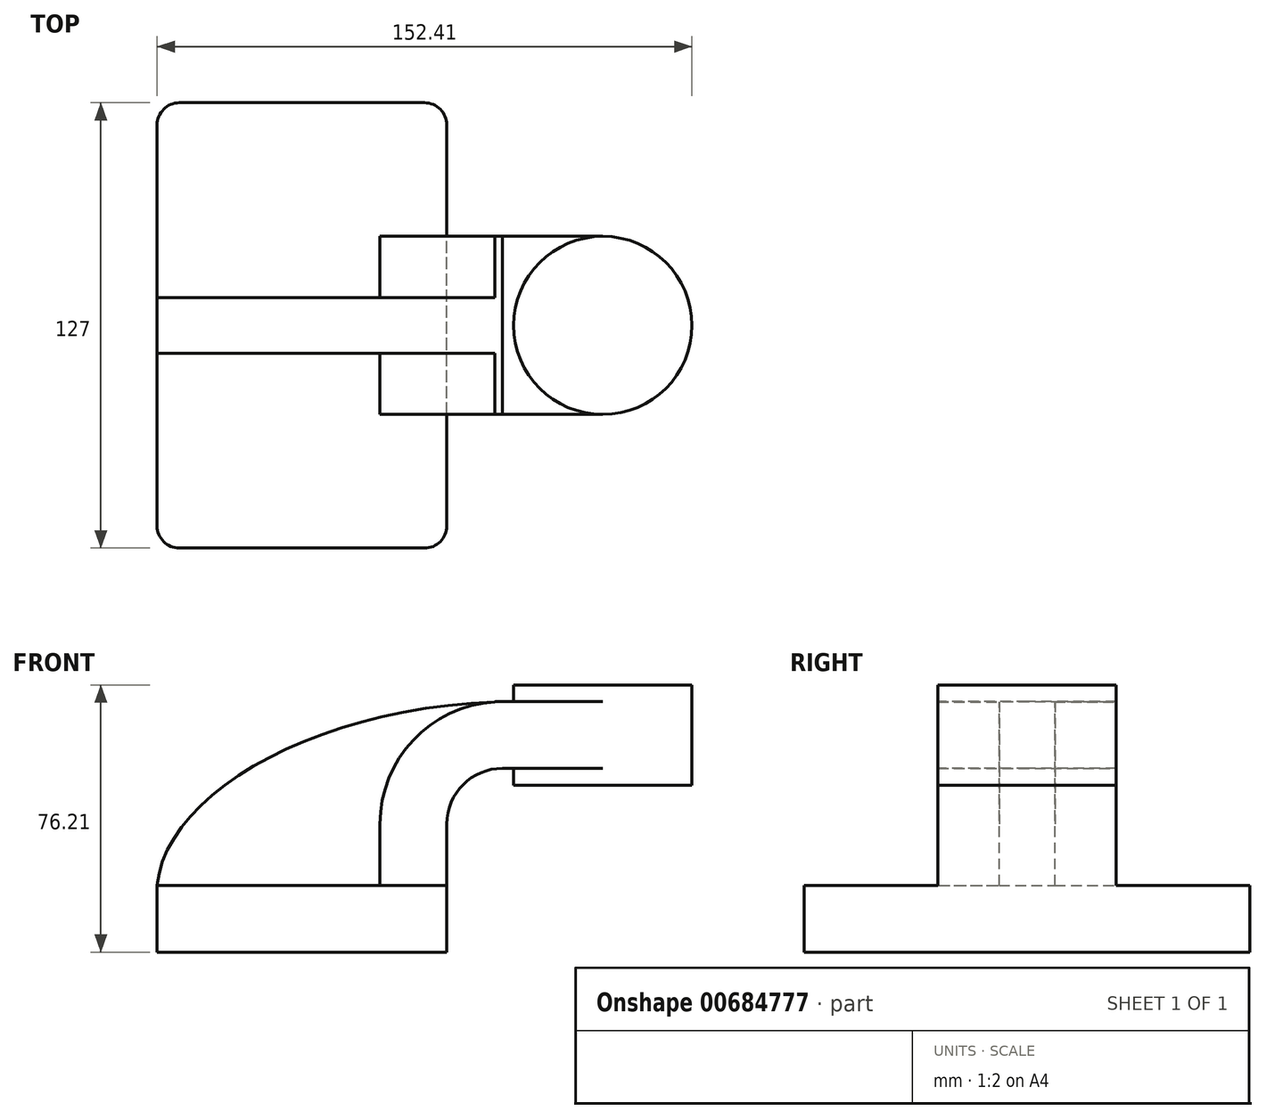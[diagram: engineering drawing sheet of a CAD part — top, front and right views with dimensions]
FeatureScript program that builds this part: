
annotation { "Feature Type Name" : "Feature", "Feature Type Description" : "" }
export const myFeature = defineFeature(function(context is Context, id is Id, definition is map)
    precondition{}
    {
        {
            var Q0;
            Q0=qCreatedBy(makeId("Front.planeOp"),FACE);
            var sketch = newSketch(context, id + "F0", { "sketchPlane" : qUnion([Q0])});
            skLineSegment(sketch, "E0.bottom", {"start": v(41.28, -9.52) * mm, "end": v(-41.28, -9.52) * mm});
            skLineSegment(sketch, "E0.top", {"start": v(41.28, 9.53) * mm, "end": v(-41.28, 9.53) * mm});
            skLineSegment(sketch, "E0.left", {"start": v(41.28, -9.52) * mm, "end": v(41.28, 9.53) * mm});
            skLineSegment(sketch, "E0.right", {"start": v(-41.28, -9.52) * mm, "end": v(-41.28, 9.53) * mm});
            skPoint(sketch, "E0.middle", {"position": v(0, 0) * mm});
            skLineSegment(sketch, "E1.bottom", {"start": v(111.13, 38.1) * mm, "end": v(60.33, 38.1) * mm});
            skLineSegment(sketch, "E1.top", {"start": v(111.13, 66.68) * mm, "end": v(60.33, 66.68) * mm});
            skLineSegment(sketch, "E1.left", {"start": v(111.13, 38.1) * mm, "end": v(111.13, 66.68) * mm});
            skLineSegment(sketch, "E1.right", {"start": v(60.33, 38.1) * mm, "end": v(60.33, 66.68) * mm});
            skPoint(sketch, "E1.middle", {"position": v(85.73, 52.39) * mm});
            skLineSegment(sketch, "E2", {"start": v(41.28, 9.53) * mm, "end": v(41.28, 27) * mm});
            skArc(sketch, "E3", {"start": v(41.27, 27) * mm, "mid": v(45.92, 38.23) * mm, "end": v(57.15, 42.88) * mm});
            skLineSegment(sketch, "E4", {"start": v(57.15, 42.88) * mm, "end": v(85.73, 42.88) * mm});
            skLineSegment(sketch, "E5.0", {"start": v(57.15, 61.93) * mm, "end": v(85.73, 61.93) * mm});
            skArc(sketch, "E5.1", {"start": v(22.23, 27) * mm, "mid": v(32.45, 51.7) * mm, "end": v(57.15, 61.93) * mm});
            skLineSegment(sketch, "E5.2", {"start": v(22.22, 9.53) * mm, "end": v(22.22, 27) * mm});
            skLineSegment(sketch, "E6", {"start": v(85.73, 38.1) * mm, "end": v(85.73, 66.68) * mm});
            skFitSpline(sketch, "E7", {"points": [v(-41.28, 9.52) * mm, v(57.15, 61.93) * mm], "startDerivative": vector(7.78, 79.46) * mm, "endDerivative": vector(158.17, 4.1) * mm});
            skSolve(sketch);
        }
        {
            var Q0;
            Q0=makeQuery(id+"F0.imprint","IMPRINT",FACE,{"disambiguationData":[TD([[makeQuery(id+"F0.imprint","IMPRINT",EDGE,{"derivedFrom":sQuery(id+"F0.wireOp",EDGE,"E0.bottom")}),-1.0]])]});
            extrude(context, id + "F1", {"entities" : qUnion([Q0]), "endBound" : BoundingType.SYMMETRIC, "depth" : 127 * mm, "offsetDistance" : 25.4 * mm});
        }
        {
            var Q0;
            {var subQ1=sQuery(id+"F0.wireOp",EDGE,"E2");Q0=makeQuery(id+"F0.imprint","IMPRINT",FACE,{"disambiguationData":[TD([[makeQuery(id+"F0.imprint","IMPRINT",EDGE,{"derivedFrom":subQ1}),1.0]])]});}
            extrude(context, id + "F2", {"entities" : qUnion([Q0]), "operationType" : NewBodyOperationType.ADD, "endBound" : BoundingType.SYMMETRIC, "depth" : 50.8 * mm, "offsetDistance" : 25.4 * mm});
        }
        {
            var Q0;
            {var subQ0=sQuery(id+"F0.wireOp",EDGE,"E4");var subQ1=sQuery(id+"F0.wireOp",EDGE,"E1.right");var subQ2=makeQuery(id+"F0.imprint","INTERSECT",VERTEX,{"derivedFrom":[subQ1,subQ0]});Q0=makeQuery(id+"F0.imprint","IMPRINT",FACE,{"disambiguationData":[TD([[makeQuery(id+"F0.imprint","IMPRINT",EDGE,{"disambiguationData":[TD([[subQ2,-1.0]])],"derivedFrom":subQ1}),-1.0]])]});}
            extrude(context, id + "F3", {"entities" : qUnion([Q0]), "operationType" : NewBodyOperationType.ADD, "endBound" : BoundingType.SYMMETRIC, "depth" : 50.8 * mm, "offsetDistance" : 25.4 * mm});
        }
        {
            var Q0;
            {var subQ3=sQuery(id+"F0.wireOp",EDGE,"E5.2");Q0=makeQuery(id+"F0.imprint","IMPRINT",FACE,{"disambiguationData":[TD([[makeQuery(id+"F0.imprint","IMPRINT",EDGE,{"derivedFrom":subQ3}),1.0]])]});}
            extrude(context, id + "F4", {"entities" : qUnion([Q0]), "operationType" : NewBodyOperationType.ADD, "endBound" : BoundingType.SYMMETRIC, "depth" : 15.88 * mm, "offsetDistance" : 25.4 * mm});
        }
        {
            var Q0;
            {var subQ0=sQuery(id+"F0.wireOp",EDGE,"E1.left");Q0=makeQuery(id+"F0.imprint","IMPRINT",FACE,{"disambiguationData":[TD([[makeQuery(id+"F0.imprint","IMPRINT",EDGE,{"derivedFrom":subQ0}),1.0]])]});}
            var Q1;
            Q1=sQuery(id+"F0.wireOp",EDGE,"E6");
            revolve(context, id + "F5", {"operationType" : NewBodyOperationType.ADD, "surfaceOperationType" : NewSurfaceOperationType.NEW, "entities" : qUnion([Q0]), "axis" : qUnion([Q1]), "revolveType" : RevolveType.FULL});
        }
        {
            var Q0;
            Q0=makeQuery(id+"F1.opExtrude","CAP_EDGE",EDGE,{"disambiguationData":[OSD([sQuery(id+"F0.wireOp",EDGE,"E0.right")])],"isStart":false});
            var Q1;
            Q1=makeQuery(id+"F1.opExtrude","CAP_EDGE",EDGE,{"disambiguationData":[OSD([sQuery(id+"F0.wireOp",EDGE,"E0.left")])],"isStart":false});
            var Q2;
            Q2=makeQuery(id+"F1.opExtrude","CAP_EDGE",EDGE,{"disambiguationData":[OSD([sQuery(id+"F0.wireOp",EDGE,"E0.left")])],"isStart":true});
            var Q3;
            Q3=makeQuery(id+"F1.opExtrude","CAP_EDGE",EDGE,{"disambiguationData":[OSD([sQuery(id+"F0.wireOp",EDGE,"E0.right")])],"isStart":true});
            fillet(context, id + "F6", {"entities" : qUnion([Q0, Q1, Q2, Q3]), "radius" : 6.35 * mm, "tangentPropagation" : true, "allowEdgeOverflow" : false});
        }
    });
